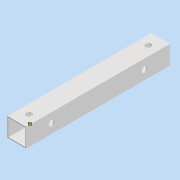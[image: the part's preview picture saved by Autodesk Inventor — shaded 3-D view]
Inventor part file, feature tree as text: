
AUTODESK INVENTOR PART (.ipt)
format: ipt  version: 2020 (Build 240168000, 168)  size: 130,048 bytes
history: native  units: mm
features: sketch x3, hole x2, extrude x1
ambient origin geometry x8: Origin, YZ Plane, XZ Plane, XY Plane, X Axis, Y Axis, Z Axis, Center Point
bodies: Solido1 (feature_tree)
feature tree (6):
  extrude  "Estrusione1"  Depth=20.0mm
  hole  "Foro7"  [1 undecoded]
  hole  "Foro8"  [1 undecoded]
  sketch  "Schizzo1"
  sketch  "Schizzo8"
  sketch  "Schizzo9"
note: 2 required parameter values undecoded (feature->parameter linkage not recoverable at this tier; creation-order binding heuristic only, values carry confidence <= 0.55)
